# Revit family: Сопрано
name_source: partatom
category: Осветительные приборы
units: mm (PartAtom-declared; Revit-internal decimal feet)

## family parameters
Всегда вертикально = Да
Источник света = Да
На основе рабочей плоскости = Нет
Общий = Нет
При загрузке вырезать с полостями = Нет
Размер круглого соединителя = Использовать диаметр
Тип детали = Нормальный
Точка расчета площади = Нет

## types (1)
- Сопрано
    ADSK_URL страницы изделия = https://www.allfresco.ru
    ADSK_Артикул = ДТУ160с1
    ADSK_Единица измерения = шт.
    ADSK_Завод-изготовитель = ALFRESCO
    ADSK_Количество фаз = 2
    ADSK_Количество фаз числовое = 0
    ADSK_Коэффициент мощности = 0
    ADSK_Масса = 253
    ADSK_Масса_Текст = 253
    ADSK_Модель = Сопрано ДТУ-160-AF
    ADSK_Наименование = ДТУ160с1 Светодиодный светильник Сопрано ДТУ-160-AF-144Вт-9.0-6-Spot-05-24Вт
    ADSK_Напряжение = 220 В
    ADSK_Номинальная мощность = 144 Вт
    ADSK_Полная мощность = 0 В·А
    ADSK_Размер_Высота = 9000 мм
    ADSK_Ток = 0 А
    ADSK_Фактическая мощность = 140 Вт
    ADSK_Энергоэффективность = 110 лм/Вт
    D = 60 мм
    H1 = 2230 мм
    H10 = 600 мм
    H11 = 600 мм
    H12 = 600 мм
    H2 = 200 мм
    H3 = 200 мм
    H4 = 405 мм
    H5 = 395 мм
    H6 = 815 мм
    H7 = 1185 мм
    H8 = 630 мм
    H9 = 600 мм
    H_конечной точки = 1500 мм
    H_нижние столбы = 5500 мм
    H_стены = 2000 мм
    H_столбы = 9000 мм
    IP Class = IP 67
    L = 500 мм
    L1 = 547 мм
    L_отступ до конечной точки = 1500 мм
    L_отступ до центра = 1000 мм
    Блок аварийного питания = Нет
    Класс защиты = 1
    Класс пожароопасности = F (светильники предназначены для установки непосредственно на поверхность из нормально воспламеняемых материалов)
    Климатическая зона = УХЛ1
    Короб_Диаметр = 20 мм
    Корпус светильника = Антрацит
    Материал рассеивателя = Светотехнический ПК
    Область использования = Парки, скверы, общественные пространства, городская инфраструктура
    Полная установленная мощность = 0 В·А
    Рассеиватель = Серебро
    Светофильтр = 16777215
    Смещение цветовой температуры при затухании лампы = <Нет>
    Таблица выбора = Таблица параметров светильников_par3_v1
    Температура эксплуатации = -40 +50
    Тип ИС = LED-модуль
    Тип КСС = тип Г (глубокая)
    Тип ПРА = -
    Тип продукции = LED-светильник
    Угол наклона = 60.00°
    Файл фотометрической сетки = Spot-05-AF 24W 60°.ies
    Цветоывая температура = 2700-5500

## geometry (parser evidence)
native form markers: Blend x2
no freeform markers — native parametric forms only
